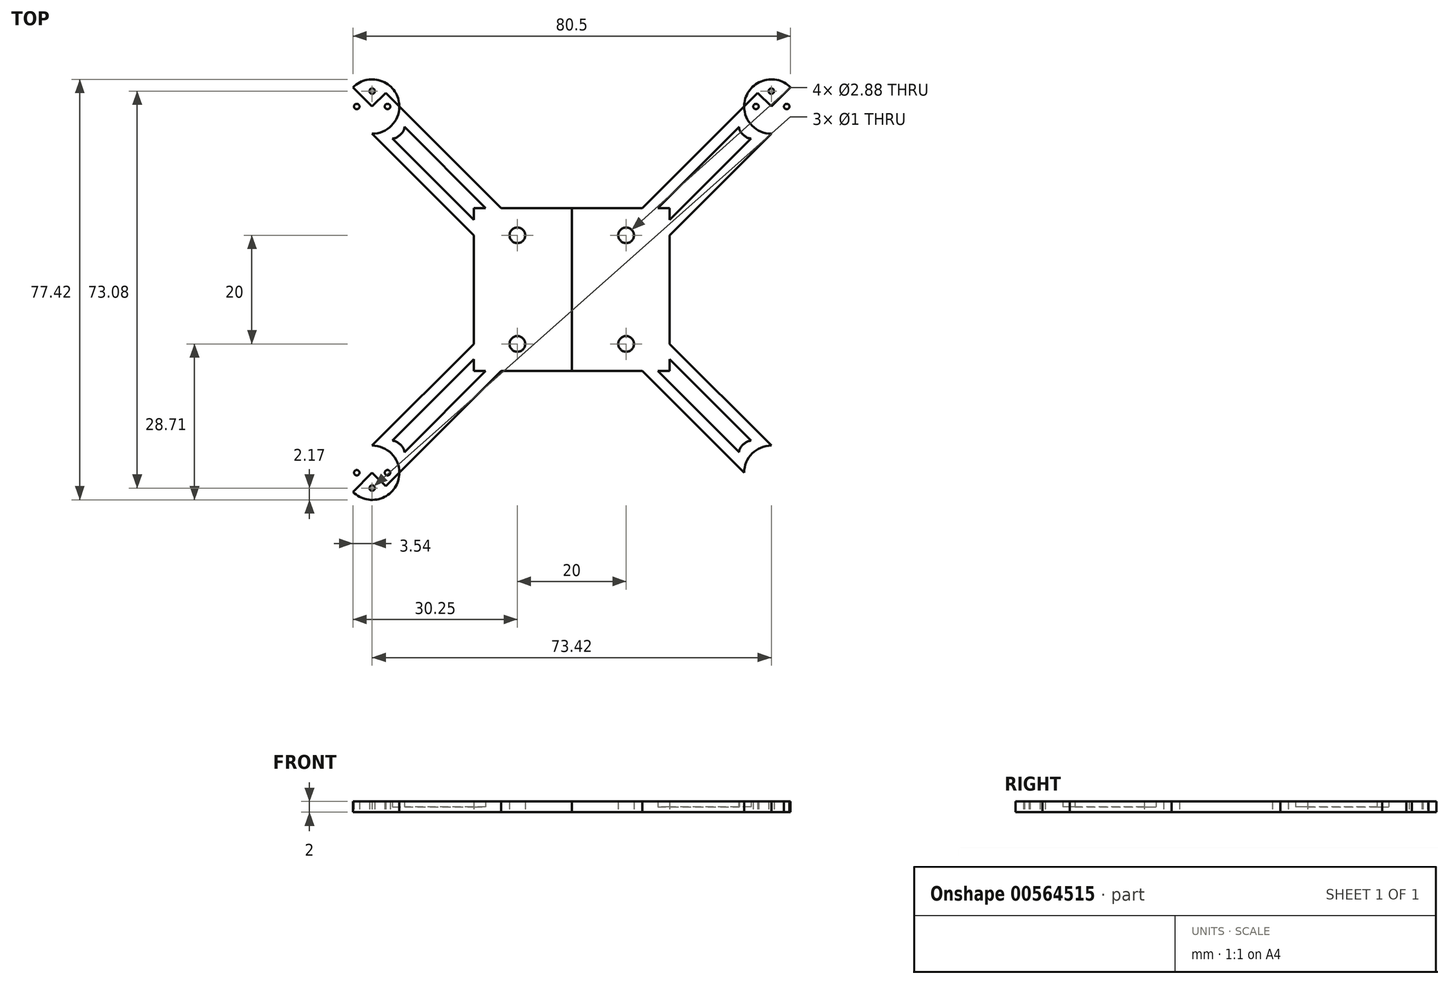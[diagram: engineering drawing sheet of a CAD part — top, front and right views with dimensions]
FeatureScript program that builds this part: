
annotation { "Feature Type Name" : "Feature", "Feature Type Description" : "" }
export const myFeature = defineFeature(function(context is Context, id is Id, definition is map)
    precondition{}
    {
        {
            var Q0;
            Q0=qCreatedBy(makeId("Top.planeOp"),FACE);
            var sketch = newSketch(context, id + "F0", { "sketchPlane" : qUnion([Q0])});
            skLineSegment(sketch, "E0.bottom", {"start": v(-18, 15) * mm, "end": v(0, 15) * mm});
            skLineSegment(sketch, "E0.top", {"start": v(-18, 0) * mm, "end": v(0, 0) * mm});
            skLineSegment(sketch, "E0.left", {"start": v(-18, 15) * mm, "end": v(-18, 0) * mm});
            skLineSegment(sketch, "E0.right", {"start": v(0, 15) * mm, "end": v(0, 0) * mm});
            skCircle(sketch, "E1", {"center": v(-36.71, 33.71) * mm, "radius": 5 * mm});
            skLineSegment(sketch, "E2", {"start": v(-18, 10) * mm, "end": v(-39.21, 31.21) * mm});
            skLineSegment(sketch, "E3", {"start": v(-39.21, 31.21) * mm, "end": v(-34.21, 36.21) * mm});
            skLineSegment(sketch, "E4", {"start": v(-34.21, 36.21) * mm, "end": v(-13, 15) * mm});
            skLineSegment(sketch, "E5", {"start": v(-13, 15) * mm, "end": v(-18, 10) * mm});
            skCircle(sketch, "E6", {"center": v(-36.71, 36.54) * mm, "radius": 0.5 * mm});
            skLineSegment(sketch, "E7", {"start": v(-32.97, 27.8) * mm, "end": v(-18, 12.83) * mm});
            skLineSegment(sketch, "E8", {"start": v(-18, 12.83) * mm, "end": v(-18, 15) * mm});
            skLineSegment(sketch, "E9", {"start": v(-15.83, 15) * mm, "end": v(-18, 15) * mm});
            skLineSegment(sketch, "E10", {"start": v(-15.83, 15) * mm, "end": v(-30.8, 29.97) * mm});
            skFitSpline(sketch, "E11", {"points": [v(-32.97, 27.8) * mm, v(-30.8, 29.97) * mm], "startDerivative": vector(2.9, 0.08) * mm, "endDerivative": vector(-0.55, 2.6) * mm});
            skLineSegment(sketch, "E12", {"start": v(-40.25, 37.25) * mm, "end": v(-33.18, 30.18) * mm});
            skCircle(sketch, "E13.MirrorC", {"center": v(-39.54, 33.71) * mm, "radius": 0.5 * mm});
            skLineSegment(sketch, "E14.MirrorCS", {"start": v(-34.21, 36.21) * mm, "end": v(-39.21, 31.21) * mm});
            skCircle(sketch, "E15.MirrorC", {"center": v(-36.71, 30.88) * mm, "radius": 0.5 * mm});
            skCircle(sketch, "E16.MirrorC", {"center": v(-33.88, 33.71) * mm, "radius": 0.5 * mm});
            skCircle(sketch, "E17", {"center": v(-10, 10) * mm, "radius": 1.44 * mm});
            skSolve(sketch);
        }
        {
            var Q0;
            {var subQ6=sQuery(id+"F0.wireOp",EDGE,"E7");Q0=makeQuery(id+"F0.imprint","IMPRINT",FACE,{"disambiguationData":[TD([[makeQuery(id+"F0.imprint","IMPRINT",EDGE,{"derivedFrom":subQ6}),-1.0]])]});}
            var Q1;
            {var subQ2=sQuery(id+"F0.wireOp",EDGE,"E0.top");Q1=makeQuery(id+"F0.imprint","IMPRINT",FACE,{"disambiguationData":[TD([[makeQuery(id+"F0.imprint","IMPRINT",EDGE,{"derivedFrom":subQ2}),1.0]])]});}
            var Q2;
            {var subQ1=sQuery(id+"F0.wireOp",EDGE,"E5");Q2=makeQuery(id+"F0.imprint","IMPRINT",FACE,{"disambiguationData":[TD([[makeQuery(id+"F0.imprint","IMPRINT",EDGE,{"derivedFrom":subQ1}),-1.0]])]});}
            var Q3;
            Q3=makeQuery(id+"F0.imprint","IMPRINT",FACE,{"disambiguationData":[TD([[makeQuery(id+"F0.imprint","IMPRINT",EDGE,{"derivedFrom":sQuery(id+"F0.wireOp",EDGE,"E16.MirrorC")}),1.0]])]});
            var Q4;
            Q4=makeQuery(id+"F0.imprint","IMPRINT",FACE,{"disambiguationData":[TD([[makeQuery(id+"F0.imprint","IMPRINT",EDGE,{"derivedFrom":sQuery(id+"F0.wireOp",EDGE,"E6")}),-1.0]])]});
            var Q5;
            Q5=makeQuery(id+"F0.imprint","IMPRINT",FACE,{"disambiguationData":[TD([[makeQuery(id+"F0.imprint","IMPRINT",EDGE,{"derivedFrom":sQuery(id+"F0.wireOp",EDGE,"E7")}),1.0]])]});
            var Q6;
            Q6=makeQuery(id+"F0.imprint","IMPRINT",FACE,{"disambiguationData":[TD([[makeQuery(id+"F0.imprint","IMPRINT",EDGE,{"derivedFrom":sQuery(id+"F0.wireOp",EDGE,"E15.MirrorC")}),-1.0]])]});
            var Q7;
            Q7=makeQuery(id+"F0.imprint","IMPRINT",FACE,{"disambiguationData":[TD([[makeQuery(id+"F0.imprint","IMPRINT",EDGE,{"derivedFrom":sQuery(id+"F0.wireOp",EDGE,"E13.MirrorC")}),1.0]])]});
            var Q8;
            Q8=makeQuery(id+"F0.imprint","IMPRINT",FACE,{"disambiguationData":[TD([[makeQuery(id+"F0.imprint","IMPRINT",EDGE,{"derivedFrom":sQuery(id+"F0.wireOp",EDGE,"E15.MirrorC")}),1.0]])]});
            var Q9;
            Q9=makeQuery(id+"F0.imprint","IMPRINT",FACE,{"disambiguationData":[TD([[makeQuery(id+"F0.imprint","IMPRINT",EDGE,{"derivedFrom":sQuery(id+"F0.wireOp",EDGE,"E16.MirrorC")}),-1.0]])]});
            var Q10;
            Q10=makeQuery(id+"F0.imprint","IMPRINT",FACE,{"disambiguationData":[TD([[makeQuery(id+"F0.imprint","IMPRINT",EDGE,{"derivedFrom":sQuery(id+"F0.wireOp",EDGE,"E13.MirrorC")}),-1.0]])]});
            var Q11;
            Q11=makeQuery(id+"F0.imprint","IMPRINT",FACE,{"disambiguationData":[TD([[makeQuery(id+"F0.imprint","IMPRINT",EDGE,{"derivedFrom":sQuery(id+"F0.wireOp",EDGE,"E6")}),1.0]])]});
            extrude(context, id + "F1", {"entities" : qUnion([Q0, Q1, Q2, Q3, Q4, Q5, Q6, Q7, Q8, Q9, Q10, Q11]), "endBound" : BoundingType.SYMMETRIC, "depth" : 2 * mm, "offsetDistance" : 25 * mm});
        }
        {
            var Q0;
            Q0=makeQuery(id+"F0.imprint","IMPRINT",FACE,{"disambiguationData":[TD([[makeQuery(id+"F0.imprint","IMPRINT",EDGE,{"derivedFrom":sQuery(id+"F0.wireOp",EDGE,"E13.MirrorC")}),-1.0]])]});
            var Q1;
            Q1=makeQuery(id+"F0.imprint","IMPRINT",FACE,{"disambiguationData":[TD([[makeQuery(id+"F0.imprint","IMPRINT",EDGE,{"derivedFrom":sQuery(id+"F0.wireOp",EDGE,"E6")}),1.0]])]});
            var Q2;
            Q2=makeQuery(id+"F0.imprint","IMPRINT",FACE,{"disambiguationData":[TD([[makeQuery(id+"F0.imprint","IMPRINT",EDGE,{"derivedFrom":sQuery(id+"F0.wireOp",EDGE,"E16.MirrorC")}),-1.0]])]});
            var Q3;
            Q3=makeQuery(id+"F0.imprint","IMPRINT",FACE,{"disambiguationData":[TD([[makeQuery(id+"F0.imprint","IMPRINT",EDGE,{"derivedFrom":sQuery(id+"F0.wireOp",EDGE,"E15.MirrorC")}),1.0]])]});
            extrude(context, id + "F2", {"entities" : qUnion([Q0, Q1, Q2, Q3]), "operationType" : NewBodyOperationType.REMOVE, "endBound" : BoundingType.SYMMETRIC, "depth" : 25 * mm, "offsetDistance" : 25 * mm});
        }
        {
            var Q0;
            Q0=makeQuery(id+"F0.imprint","IMPRINT",FACE,{"disambiguationData":[TD([[makeQuery(id+"F0.imprint","IMPRINT",EDGE,{"derivedFrom":sQuery(id+"F0.wireOp",EDGE,"E7")}),1.0]])]});
            extrude(context, id + "F3", {"entities" : qUnion([Q0]), "operationType" : NewBodyOperationType.REMOVE, "depth" : 1 * mm, "offsetDistance" : 25 * mm});
        }
        {
            var Q0;
            Q0=makeQuery(id+"F1.opExtrude","SWEPT_BODY",BODY,{"disambiguationData":[OSD([sQuery(id+"F0.wireOp",EDGE,"E0.bottom"),sQuery(id+"F0.wireOp",EDGE,"E0.top"),sQuery(id+"F0.wireOp",EDGE,"E0.left"),sQuery(id+"F0.wireOp",EDGE,"E0.right"),sQuery(id+"F0.wireOp",EDGE,"E1"),sQuery(id+"F0.wireOp",EDGE,"E2"),sQuery(id+"F0.wireOp",EDGE,"E4"),sQuery(id+"F0.wireOp",EDGE,"E17")])]});
            var Q1;
            Q1=qCreatedBy(makeId("Front.planeOp"),FACE);
            mirror(context, id + "F4", {"operationType" : NewBodyOperationType.ADD, "entities" : qUnion([Q0]), "mirrorPlane" : qUnion([Q1])});
        }
        {
            var Q0;
            Q0=makeQuery(id+"F1.opExtrude","SWEPT_BODY",BODY,{"disambiguationData":[OSD([sQuery(id+"F0.wireOp",EDGE,"E0.bottom"),sQuery(id+"F0.wireOp",EDGE,"E0.top"),sQuery(id+"F0.wireOp",EDGE,"E0.left"),sQuery(id+"F0.wireOp",EDGE,"E0.right"),sQuery(id+"F0.wireOp",EDGE,"E1"),sQuery(id+"F0.wireOp",EDGE,"E2"),sQuery(id+"F0.wireOp",EDGE,"E4"),sQuery(id+"F0.wireOp",EDGE,"E17")])]});
            var Q1;
            Q1=qCreatedBy(makeId("Right.planeOp"),FACE);
            mirror(context, id + "F5", {"operationType" : NewBodyOperationType.ADD, "entities" : qUnion([Q0]), "mirrorPlane" : qUnion([Q1])});
        }
    });
